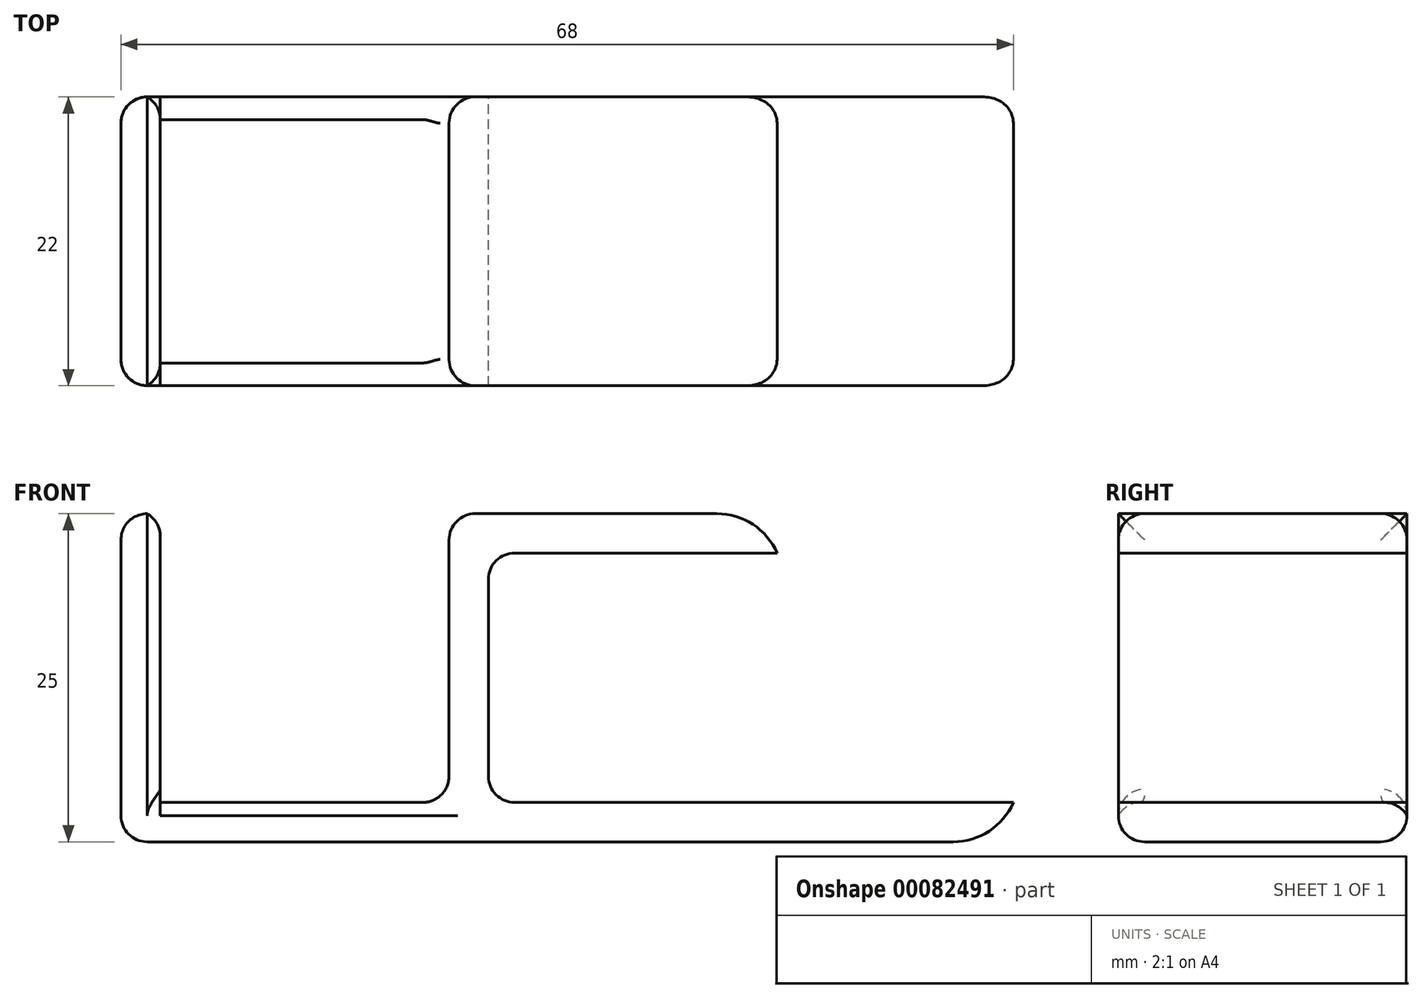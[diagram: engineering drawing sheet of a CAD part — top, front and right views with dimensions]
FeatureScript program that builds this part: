
annotation { "Feature Type Name" : "Feature", "Feature Type Description" : "" }
export const myFeature = defineFeature(function(context is Context, id is Id, definition is map)
    precondition{}
    {
        {
            assignVariable(context, id + "F0", {"name" : "totalWidth", "anyValue" : 22});
        }
        {
            var Q0;
            Q0=qCreatedBy(makeId("Front.planeOp"),FACE);
            var sketch = newSketch(context, id + "F1", { "sketchPlane" : qUnion([Q0])});
            skLineSegment(sketch, "E0.bottom", {"start": v(-34, 1.5) * mm, "end": v(34, 1.5) * mm});
            skLineSegment(sketch, "E0.top", {"start": v(-34, -1.5) * mm, "end": v(34, -1.5) * mm});
            skLineSegment(sketch, "E0.left", {"start": v(-34, 1.5) * mm, "end": v(-34, -1.5) * mm});
            skLineSegment(sketch, "E0.right", {"start": v(34, 1.5) * mm, "end": v(34, -1.5) * mm});
            skPoint(sketch, "E0.middle", {"position": v(0, 0) * mm});
            skLineSegment(sketch, "E1.bottom", {"start": v(-34, 1.5) * mm, "end": v(-31, 1.5) * mm});
            skLineSegment(sketch, "E1.top", {"start": v(-34, 23.5) * mm, "end": v(-31, 23.5) * mm});
            skLineSegment(sketch, "E1.left", {"start": v(-34, 1.5) * mm, "end": v(-34, 23.5) * mm});
            skLineSegment(sketch, "E1.right", {"start": v(-31, 1.5) * mm, "end": v(-31, 23.5) * mm});
            skLineSegment(sketch, "E2.bottom", {"start": v(-9, 1.5) * mm, "end": v(-6, 1.5) * mm});
            skLineSegment(sketch, "E2.top", {"start": v(-9, 23.5) * mm, "end": v(-6, 23.5) * mm});
            skLineSegment(sketch, "E2.left", {"start": v(-6, 1.5) * mm, "end": v(-6, 23.5) * mm});
            skLineSegment(sketch, "E2.right", {"start": v(-9, 1.5) * mm, "end": v(-9, 23.5) * mm});
            skLineSegment(sketch, "E3.bottom", {"start": v(-6, 23.5) * mm, "end": v(16, 23.5) * mm});
            skLineSegment(sketch, "E3.top", {"start": v(-6, 20.5) * mm, "end": v(16, 20.5) * mm});
            skLineSegment(sketch, "E3.left", {"start": v(-6, 23.5) * mm, "end": v(-6, 20.5) * mm});
            skLineSegment(sketch, "E3.right", {"start": v(16, 23.5) * mm, "end": v(16, 20.5) * mm});
            skSolve(sketch);
        }
        {
            var Q0;
            Q0=qSketchRegion(id+"F1",true);
            extrude(context, id + "F2", {"entities" : qUnion([Q0]), "endBound" : BoundingType.SYMMETRIC, "depth" : (getVariable(context, 'totalWidth')) * mm});
        }
        {
            var Q0;
            Q0=makeQuery(id+"F2.opExtrude","SWEPT_EDGE",EDGE,{"disambiguationData":[OSD([sQuery(id+"F1.wireOp",EDGE,"E3.bottom"),sQuery(id+"F1.wireOp",EDGE,"E3.right")])]});
            var Q1;
            Q1=makeQuery(id+"F2.opExtrude","SWEPT_EDGE",EDGE,{"disambiguationData":[OSD([sQuery(id+"F1.wireOp",EDGE,"E0.top"),sQuery(id+"F1.wireOp",EDGE,"E0.right")])]});
            fillet(context, id + "F3", {"entities" : qUnion([Q0, Q1]), "radius" : 5 * mm, "tangentPropagation" : true, "allowEdgeOverflow" : false});
        }
        {
            var Q0;
            {var subQ0=sQuery(id+"F1.wireOp",EDGE,"E2.right");var subQ2=sQuery(id+"F1.wireOp",EDGE,"E0.bottom");var subQ3=sQuery(id+"F1.wireOp",EDGE,"E2.bottom");Q0=makeQuery(id+"FIEtzXwt2S1aHH3_1.boolean.opBoolean","SPLIT",EDGE,{"disambiguationData":[TD([makeQuery(id+"FIEtzXwt2S1aHH3_1.opExtrude","SWEPT_FACE",FACE,{"disambiguationData":[OSD([sQuery(id+"Fe2C8JE01yYqcFm_1.wireOp",EDGE,"1WCNVF3C-L18H-Aqcg-mi7t-To6PXvvJ6JRQ.top")])]})])],"derivedFrom":makeQuery(id+"F2.opExtrude","SWEPT_EDGE",EDGE,{"disambiguationData":[OSD([subQ2,subQ3,subQ0])]})});}
            var Q1;
            {var subQ0=sQuery(id+"F1.wireOp",EDGE,"E2.right");var subQ2=sQuery(id+"F1.wireOp",EDGE,"E0.bottom");var subQ3=sQuery(id+"F1.wireOp",EDGE,"E2.bottom");Q1=makeQuery(id+"FIEtzXwt2S1aHH3_1.boolean.opBoolean","SPLIT",EDGE,{"disambiguationData":[TD([makeQuery(id+"FIEtzXwt2S1aHH3_1.opExtrude","SWEPT_FACE",FACE,{"disambiguationData":[OSD([sQuery(id+"Fe2C8JE01yYqcFm_1.wireOp",EDGE,"1WCNVF3C-L18H-Aqcg-mi7t-To6PXvvJ6JRQ.bottom")])]})])],"derivedFrom":makeQuery(id+"F2.opExtrude","SWEPT_EDGE",EDGE,{"disambiguationData":[OSD([subQ2,subQ3,subQ0])]})});}
            fillet(context, id + "F4", {"entities" : qUnion([Q0, Q1]), "radius" : 2 * mm, "allowEdgeOverflow" : false});
        }
        {
            var Q0;
            Q0=makeQuery(id+"F2.opExtrude","SWEPT_EDGE",EDGE,{"disambiguationData":[OSD([sQuery(id+"F1.wireOp",EDGE,"E2.top"),sQuery(id+"F1.wireOp",EDGE,"E2.right")])]});
            fillet(context, id + "F5", {"entities" : qUnion([Q0]), "radius" : 2 * mm, "tangentPropagation" : true, "allowEdgeOverflow" : false});
        }
        {
            var Q0;
            Q0=makeQuery(id+"F2.opExtrude","CAP_EDGE",EDGE,{"disambiguationData":[OSD([sQuery(id+"F1.wireOp",EDGE,"E2.top"),sQuery(id+"F1.wireOp",EDGE,"E3.bottom")])],"isStart":false});
            var Q1;
            Q1=makeQuery(id+"F2.opExtrude","CAP_EDGE",EDGE,{"disambiguationData":[OSD([sQuery(id+"F1.wireOp",EDGE,"E2.top"),sQuery(id+"F1.wireOp",EDGE,"E3.bottom")])],"isStart":true});
            var Q2;
            Q2=makeQuery(id+"F2.opExtrude","CAP_EDGE",EDGE,{"disambiguationData":[OSD([sQuery(id+"F1.wireOp",EDGE,"E0.top")])],"isStart":true});
            var Q3;
            Q3=makeQuery(id+"F2.opExtrude","CAP_EDGE",EDGE,{"disambiguationData":[OSD([sQuery(id+"F1.wireOp",EDGE,"E0.top")])],"isStart":false});
            var Q4;
            {var subQ1=sQuery(id+"F1.wireOp",EDGE,"E0.left");var subQ2=sQuery(id+"F1.wireOp",EDGE,"E0.top");Q4=makeQuery(id+"FIEtzXwt2S1aHH3_1.boolean.opBoolean","SPLIT",EDGE,{"disambiguationData":[TD([makeQuery(id+"FIEtzXwt2S1aHH3_1.opExtrude","SWEPT_FACE",FACE,{"disambiguationData":[OSD([sQuery(id+"Fe2C8JE01yYqcFm_1.wireOp",EDGE,"1WCNVF3C-L18H-Aqcg-mi7t-To6PXvvJ6JRQ.bottom")])]})])],"derivedFrom":makeQuery(id+"F2.opExtrude","SWEPT_EDGE",EDGE,{"disambiguationData":[OSD([subQ2,subQ1])]})});}
            var Q5;
            {var subQ1=sQuery(id+"F1.wireOp",EDGE,"E0.left");var subQ2=sQuery(id+"F1.wireOp",EDGE,"E0.top");Q5=makeQuery(id+"FIEtzXwt2S1aHH3_1.boolean.opBoolean","SPLIT",EDGE,{"disambiguationData":[TD([makeQuery(id+"FIEtzXwt2S1aHH3_1.opExtrude","SWEPT_FACE",FACE,{"disambiguationData":[OSD([sQuery(id+"Fe2C8JE01yYqcFm_1.wireOp",EDGE,"1WCNVF3C-L18H-Aqcg-mi7t-To6PXvvJ6JRQ.top")])]})])],"derivedFrom":makeQuery(id+"F2.opExtrude","SWEPT_EDGE",EDGE,{"disambiguationData":[OSD([subQ2,subQ1])]})});}
            var Q6;
            Q6=makeQuery(id+"FIEtzXwt2S1aHH3_1.boolean.opBoolean","INTERSECT",EDGE,{"derivedFrom":[makeQuery(id+"F2.opExtrude","SWEPT_FACE",FACE,{"disambiguationData":[OSD([sQuery(id+"F1.wireOp",EDGE,"E0.top")])]}),makeQuery(id+"FIEtzXwt2S1aHH3_1.opExtrude","SWEPT_FACE",FACE,{"disambiguationData":[OSD([sQuery(id+"Fe2C8JE01yYqcFm_1.wireOp",EDGE,"1WCNVF3C-L18H-Aqcg-mi7t-To6PXvvJ6JRQ.top")])]})]});
            var Q7;
            Q7=makeQuery(id+"FIEtzXwt2S1aHH3_1.boolean.opBoolean","INTERSECT",EDGE,{"derivedFrom":[makeQuery(id+"F2.opExtrude","SWEPT_FACE",FACE,{"disambiguationData":[OSD([sQuery(id+"F1.wireOp",EDGE,"E0.top")])]}),makeQuery(id+"FIEtzXwt2S1aHH3_1.opExtrude","SWEPT_FACE",FACE,{"disambiguationData":[OSD([sQuery(id+"Fe2C8JE01yYqcFm_1.wireOp",EDGE,"1WCNVF3C-L18H-Aqcg-mi7t-To6PXvvJ6JRQ.bottom")])]})]});
            var Q8;
            Q8=makeQuery(id+"FIEtzXwt2S1aHH3_1.boolean.opBoolean","INTERSECT",EDGE,{"derivedFrom":[makeQuery(id+"F2.opExtrude","SWEPT_FACE",FACE,{"disambiguationData":[OSD([sQuery(id+"F1.wireOp",EDGE,"E0.top")])]}),makeQuery(id+"FIEtzXwt2S1aHH3_1.opExtrude","SWEPT_FACE",FACE,{"disambiguationData":[OSD([sQuery(id+"Fe2C8JE01yYqcFm_1.wireOp",EDGE,"1WCNVF3C-L18H-Aqcg-mi7t-To6PXvvJ6JRQ.left")])]})]});
            fillet(context, id + "F6", {"entities" : qUnion([Q0, Q1, Q2, Q3, Q4, Q5, Q6, Q7, Q8]), "radius" : 2 * mm, "tangentPropagation" : true, "allowEdgeOverflow" : false});
        }
        {
            var Q0;
            {var subQ0=sQuery(id+"F1.wireOp",EDGE,"E1.left");var subQ1=sQuery(id+"F1.wireOp",EDGE,"E1.top");Q0=makeQuery(id+"FIEtzXwt2S1aHH3_1.boolean.opBoolean","SPLIT",EDGE,{"disambiguationData":[TD([makeQuery(id+"FIEtzXwt2S1aHH3_1.opExtrude","SWEPT_FACE",FACE,{"disambiguationData":[OSD([sQuery(id+"Fe2C8JE01yYqcFm_1.wireOp",EDGE,"1WCNVF3C-L18H-Aqcg-mi7t-To6PXvvJ6JRQ.bottom")])]})])],"derivedFrom":makeQuery(id+"F2.opExtrude","SWEPT_EDGE",EDGE,{"disambiguationData":[OSD([subQ1,subQ0])]})});}
            var Q1;
            {var subQ0=sQuery(id+"F1.wireOp",EDGE,"E1.left");var subQ1=sQuery(id+"F1.wireOp",EDGE,"E1.top");Q1=makeQuery(id+"FIEtzXwt2S1aHH3_1.boolean.opBoolean","SPLIT",EDGE,{"disambiguationData":[TD([makeQuery(id+"FIEtzXwt2S1aHH3_1.opExtrude","SWEPT_FACE",FACE,{"disambiguationData":[OSD([sQuery(id+"Fe2C8JE01yYqcFm_1.wireOp",EDGE,"1WCNVF3C-L18H-Aqcg-mi7t-To6PXvvJ6JRQ.top")])]})])],"derivedFrom":makeQuery(id+"F2.opExtrude","SWEPT_EDGE",EDGE,{"disambiguationData":[OSD([subQ1,subQ0])]})});}
            var Q2;
            Q2=makeQuery(id+"FIEtzXwt2S1aHH3_1.boolean.opBoolean","INTERSECT",EDGE,{"derivedFrom":[makeQuery(id+"F2.opExtrude","SWEPT_FACE",FACE,{"disambiguationData":[OSD([sQuery(id+"F1.wireOp",EDGE,"E0.left"),sQuery(id+"F1.wireOp",EDGE,"E1.left")])]}),makeQuery(id+"FIEtzXwt2S1aHH3_1.opExtrude","SWEPT_FACE",FACE,{"disambiguationData":[OSD([sQuery(id+"Fe2C8JE01yYqcFm_1.wireOp",EDGE,"1WCNVF3C-L18H-Aqcg-mi7t-To6PXvvJ6JRQ.top")])]})]});
            var Q3;
            Q3=makeQuery(id+"F2.opExtrude","CAP_EDGE",EDGE,{"disambiguationData":[OSD([sQuery(id+"F1.wireOp",EDGE,"E0.left"),sQuery(id+"F1.wireOp",EDGE,"E1.left")])],"isStart":false});
            var Q4;
            Q4=makeQuery(id+"F2.opExtrude","CAP_EDGE",EDGE,{"disambiguationData":[OSD([sQuery(id+"F1.wireOp",EDGE,"E0.left"),sQuery(id+"F1.wireOp",EDGE,"E1.left")])],"isStart":true});
            var Q5;
            Q5=makeQuery(id+"FIEtzXwt2S1aHH3_1.boolean.opBoolean","INTERSECT",EDGE,{"derivedFrom":[makeQuery(id+"F2.opExtrude","SWEPT_FACE",FACE,{"disambiguationData":[OSD([sQuery(id+"F1.wireOp",EDGE,"E0.left"),sQuery(id+"F1.wireOp",EDGE,"E1.left")])]}),makeQuery(id+"FIEtzXwt2S1aHH3_1.opExtrude","SWEPT_FACE",FACE,{"disambiguationData":[OSD([sQuery(id+"Fe2C8JE01yYqcFm_1.wireOp",EDGE,"1WCNVF3C-L18H-Aqcg-mi7t-To6PXvvJ6JRQ.bottom")])]})]});
            fillet(context, id + "F7", {"entities" : qUnion([Q0, Q1, Q2, Q3, Q4, Q5]), "radius" : 2 * mm, "tangentPropagation" : true, "allowEdgeOverflow" : false});
        }
        {
            var Q0;
            {var subQ0=sQuery(id+"F1.wireOp",EDGE,"E1.right");var subQ1=sQuery(id+"F1.wireOp",EDGE,"E1.top");Q0=makeQuery(id+"FIEtzXwt2S1aHH3_1.boolean.opBoolean","SPLIT",EDGE,{"disambiguationData":[TD([makeQuery(id+"FIEtzXwt2S1aHH3_1.opExtrude","SWEPT_FACE",FACE,{"disambiguationData":[OSD([sQuery(id+"Fe2C8JE01yYqcFm_1.wireOp",EDGE,"1WCNVF3C-L18H-Aqcg-mi7t-To6PXvvJ6JRQ.bottom")])]})])],"derivedFrom":makeQuery(id+"F2.opExtrude","SWEPT_EDGE",EDGE,{"disambiguationData":[OSD([subQ1,subQ0])]})});}
            var Q1;
            {var subQ0=sQuery(id+"F1.wireOp",EDGE,"E1.right");var subQ1=sQuery(id+"F1.wireOp",EDGE,"E1.top");Q1=makeQuery(id+"FIEtzXwt2S1aHH3_1.boolean.opBoolean","SPLIT",EDGE,{"disambiguationData":[TD([makeQuery(id+"FIEtzXwt2S1aHH3_1.opExtrude","SWEPT_FACE",FACE,{"disambiguationData":[OSD([sQuery(id+"Fe2C8JE01yYqcFm_1.wireOp",EDGE,"1WCNVF3C-L18H-Aqcg-mi7t-To6PXvvJ6JRQ.top")])]})])],"derivedFrom":makeQuery(id+"F2.opExtrude","SWEPT_EDGE",EDGE,{"disambiguationData":[OSD([subQ1,subQ0])]})});}
            var Q2;
            Q2=makeQuery(id+"FIEtzXwt2S1aHH3_1.boolean.opBoolean","INTERSECT",EDGE,{"derivedFrom":[makeQuery(id+"F2.opExtrude","SWEPT_FACE",FACE,{"disambiguationData":[OSD([sQuery(id+"F1.wireOp",EDGE,"E1.right")])]}),makeQuery(id+"FIEtzXwt2S1aHH3_1.opExtrude","SWEPT_FACE",FACE,{"disambiguationData":[OSD([sQuery(id+"Fe2C8JE01yYqcFm_1.wireOp",EDGE,"1WCNVF3C-L18H-Aqcg-mi7t-To6PXvvJ6JRQ.bottom")])]})]});
            var Q3;
            Q3=makeQuery(id+"F2.opExtrude","CAP_EDGE",EDGE,{"disambiguationData":[OSD([sQuery(id+"F1.wireOp",EDGE,"E1.right")])],"isStart":false});
            var Q4;
            Q4=makeQuery(id+"FIEtzXwt2S1aHH3_1.boolean.opBoolean","INTERSECT",EDGE,{"derivedFrom":[makeQuery(id+"F2.opExtrude","SWEPT_FACE",FACE,{"disambiguationData":[OSD([sQuery(id+"F1.wireOp",EDGE,"E1.right")])]}),makeQuery(id+"FIEtzXwt2S1aHH3_1.opExtrude","SWEPT_FACE",FACE,{"disambiguationData":[OSD([sQuery(id+"Fe2C8JE01yYqcFm_1.wireOp",EDGE,"1WCNVF3C-L18H-Aqcg-mi7t-To6PXvvJ6JRQ.top")])]})]});
            var Q5;
            Q5=makeQuery(id+"F2.opExtrude","CAP_EDGE",EDGE,{"disambiguationData":[OSD([sQuery(id+"F1.wireOp",EDGE,"E1.right")])],"isStart":true});
            fillet(context, id + "F8", {"entities" : qUnion([Q0, Q1, Q2, Q3, Q4, Q5]), "radius" : 2 * mm, "tangentPropagation" : true, "allowEdgeOverflow" : false});
        }
        {
            var Q0;
            Q0=makeQuery(id+"F2.opExtrude","SWEPT_EDGE",EDGE,{"disambiguationData":[OSD([sQuery(id+"F1.wireOp",EDGE,"E0.bottom"),sQuery(id+"F1.wireOp",EDGE,"E2.bottom"),sQuery(id+"F1.wireOp",EDGE,"E2.left")])]});
            var Q1;
            Q1=makeQuery(id+"F2.opExtrude","SWEPT_EDGE",EDGE,{"disambiguationData":[OSD([sQuery(id+"F1.wireOp",EDGE,"E2.left"),sQuery(id+"F1.wireOp",EDGE,"E3.top"),sQuery(id+"F1.wireOp",EDGE,"E3.left")])]});
            fillet(context, id + "F9", {"entities" : qUnion([Q0, Q1]), "radius" : 2 * mm, "tangentPropagation" : true, "allowEdgeOverflow" : false});
        }
    });
